# Revit family: KS ALU-PU 80 -s-, DS 40, M10-M12, Ø108-168,3
name_source: partatom
category: HLS-Bauteile
revit_build: Autodesk Revit 2017 (Build: 20190507_1515(x64)
units: mm (PartAtom-declared; Revit-internal decimal feet)

## family parameters
Arbeitsebenenbasiert = Ja
Beim Laden mit Abzugskörper schneiden = Nein
Bemaßung runder Anschluss = Durchmesser verwenden
Gemeinsam genutzt = Ja
Immer vertikal = Nein
Raumberechnungspunkt = Nein
Teiletyp = Normal

## types (6) — shared parameters
Anschluss = M10/M12
Baustoffklasse = B2
DS = 40 mm  [stored 0.131234 ft]
DVS = 18 mm  [stored 0.0590551 ft]
Dichte Kern = 80 kg/m³
Dichte Mantel = 2.700 kg/m³
Dicke Mantel = 0,08 mm
Dämmkörper = ALU/PU
Dämmstärke = 40 mm  [stored 0.131234 ft]
Fabrikat = MEFA
Firma = MEFA Befestigungs- und Montagesysteme GmbH
HGA = 22 mm  [stored 0.0721785 ft]
Kurztext1 = Kälteschelle RG80s ALU/PU
Material = Stahl
Material Mantel = Alufolie
Materialname = S235
Mengeneinheit = St
Oberflaeche = galvanisch verzinkt
Rohrschellentyp = Maxima PSM
Vorgabe-Ansicht = 1219 mm
Wasserdampfdiffusionswiderstand = 18750 µ
Wärmeleitfähigkeit = 0.025 W/mK
max. Temperaturbeständigkeit = 120 °C
mittl. Nenndruckfestigkeit Kern = 0,5 N/mm²
stat. Belastung Kern = 0,1 N/mm²
vpe = 1 St

## per-type parameters (varying)
- Kälteschelle ALU-PU 80 -s-, DS 40, M10/M12, Ø108: A=65 mm; AB=2 mm  [stored 0.00656168 ft]; Anschlußhöhe=65 mm; Artikelnummer=75410842; B=266 mm; Breite=265 mm; D=108 mm  [stored 0.354331 ft]; D0=188 mm; DF1=35 mm  [stored 0.114829 ft]; DF2=35 mm  [stored 0.114829 ft]; Dmax=110 mm  [stored 0.360892 ft]; Dmin=106 mm  [stored 0.347769 ft]; EAN=4250928443229; Gewicht=0.75 kg; Gewicht pro Bauteil=0.75 kg; H=216 mm; Kurztext2=108 mm Iso 40 x 83 mm M10/M12; L=83 mm  [stored 0.27231 ft]; MB=30 mm  [stored 0.0984252 ft]; MD=3 mm  [stored 0.00984252 ft]; R=94 mm  [stored 0.308399 ft]; RM=97 mm  [stored 0.318241 ft]; Rohraußendurchmesser Stahl=108 mm; S=231 mm; Schalenlänge=83 mm; max. zul. Last=0.80 kN
- Kälteschelle ALU-PU 80 -s-, DS 40, M10/M12, Ø114,3: A=65 mm; AB=0 mm  [stored 0 ft]; Anschlußhöhe=65 mm; Artikelnummer=75411442; B=273 mm; Breite=271 mm; D=114 mm  [stored 0.374016 ft]; D0=194 mm; DF1=36 mm  [stored 0.11811 ft]; DF2=35 mm  [stored 0.114829 ft]; Dmax=116 mm  [stored 0.380577 ft]; Dmin=114 mm  [stored 0.374016 ft]; EAN=4250928443243; Gewicht=0.77 kg; Gewicht pro Bauteil=0.77 kg; H=222 mm; Kurztext2=114,3 mm Iso 40 x 83 mm M10/M12; L=83 mm  [stored 0.27231 ft]; MB=30 mm  [stored 0.0984252 ft]; MD=3 mm  [stored 0.00984252 ft]; R=97 mm  [stored 0.318241 ft]; RM=100 mm  [stored 0.328084 ft]; Rohraußendurchmesser Stahl=114,3 mm; S=237 mm; Schalenlänge=83 mm; max. zul. Last=0.90 kN
- Kälteschelle ALU-PU 80 -s-, DS 40, M10/M12, Ø133: A=65 mm; AB=1 mm  [stored 0.00328084 ft]; Anschlußhöhe=64 mm; Artikelnummer=76213342; B=288 mm; Breite=288 mm; D=133 mm  [stored 0.436352 ft]; D0=213 mm; DF1=34 mm; DF2=33 mm  [stored 0.108268 ft]; Dmax=135 mm  [stored 0.442913 ft]; Dmin=132 mm  [stored 0.433071 ft]; EAN=4250928444714; Gewicht=0.85 kg; Gewicht pro Bauteil=0.85 kg; H=241 mm; Kurztext2=133 mm Iso 40 x 100 mm M10/M12; L=100 mm  [stored 0.328084 ft]; MB=30 mm  [stored 0.0984252 ft]; MD=3 mm  [stored 0.00984252 ft]; R=107 mm; RM=110 mm  [stored 0.360892 ft]; Rohraußendurchmesser Stahl=133 mm; S=254 mm; Schalenlänge=100 mm; max. zul. Last=1.10 kN
- Kälteschelle ALU-PU 80 -s-, DS 40, M10/M12, Ø139,7: A=65 mm; AB=2 mm  [stored 0.00656168 ft]; Anschlußhöhe=65 mm; Artikelnummer=76214042; B=298 mm; Breite=297 mm; D=140 mm; D0=220 mm; DF1=35 mm  [stored 0.114829 ft]; DF2=35 mm  [stored 0.114829 ft]; Dmax=142 mm  [stored 0.465879 ft]; Dmin=138 mm  [stored 0.452756 ft]; EAN=4250928444752; Gewicht=0.88 kg; Gewicht pro Bauteil=0.88 kg; H=248 mm; Kurztext2=139,7 mm Iso 40 x 100 mm M10/M12; L=100 mm  [stored 0.328084 ft]; MB=30 mm  [stored 0.0984252 ft]; MD=3 mm  [stored 0.00984252 ft]; R=110 mm  [stored 0.360892 ft]; RM=113 mm; Rohraußendurchmesser Stahl=139,7 mm; S=263 mm; Schalenlänge=100 mm; max. zul. Last=1.10 kN
- Kälteschelle ALU-PU 80 -s-, DS 40, M10/M12, Ø159: A=66 mm  [stored 0.216535 ft]; AB=1 mm  [stored 0.00328084 ft]; Anschlußhöhe=65 mm; Artikelnummer=76215944; B=315 mm; Breite=315 mm; D=159 mm  [stored 0.521654 ft]; D0=239 mm; DF1=33 mm  [stored 0.108268 ft]; DF2=34 mm; Dmax=160 mm  [stored 0.524934 ft]; Dmin=158 mm; EAN=4250928444790; Gewicht=1.28 kg; Gewicht pro Bauteil=1.28 kg; H=269 mm; Kurztext2=159 mm Iso 40 x 100 mm M10/M12; L=100 mm  [stored 0.328084 ft]; MB=35 mm  [stored 0.114829 ft]; MD=4 mm  [stored 0.0131234 ft]; R=120 mm  [stored 0.393701 ft]; RM=124 mm; Rohraußendurchmesser Stahl=159 mm; S=282 mm; Schalenlänge=100 mm; max. zul. Last=1.20 kN
- Kälteschelle ALU-PU 80 -s-, DS 40, M10/M12, Ø168,3: A=66 mm  [stored 0.216535 ft]; AB=1 mm  [stored 0.00328084 ft]; Anschlußhöhe=68 mm; Artikelnummer=7621688; B=331 mm; Breite=323 mm; D=168 mm; D0=248 mm; DF1=35 mm  [stored 0.114829 ft]; DF2=36 mm  [stored 0.11811 ft]; Dmax=172 mm; Dmin=167 mm  [stored 0.5479 ft]; EAN=4250928444820; Gewicht=1.37 kg; Gewicht pro Bauteil=1.37 kg; H=278 mm; Kurztext2=168,3 mm Iso 40 x 100 mm M10/M12; L=100 mm  [stored 0.328084 ft]; MB=35 mm  [stored 0.114829 ft]; MD=4 mm  [stored 0.0131234 ft]; R=124 mm; RM=128 mm; Rohraußendurchmesser Stahl=168,3 mm; S=296 mm; Schalenlänge=100 mm; max. zul. Last=1.30 kN

note: [stored X ft] marks values corroborated as IEEE doubles in the binary element streams (Revit-internal decimal feet)

## geometry (parser evidence)
native form markers: Sweep x5
no freeform markers — native parametric forms only
